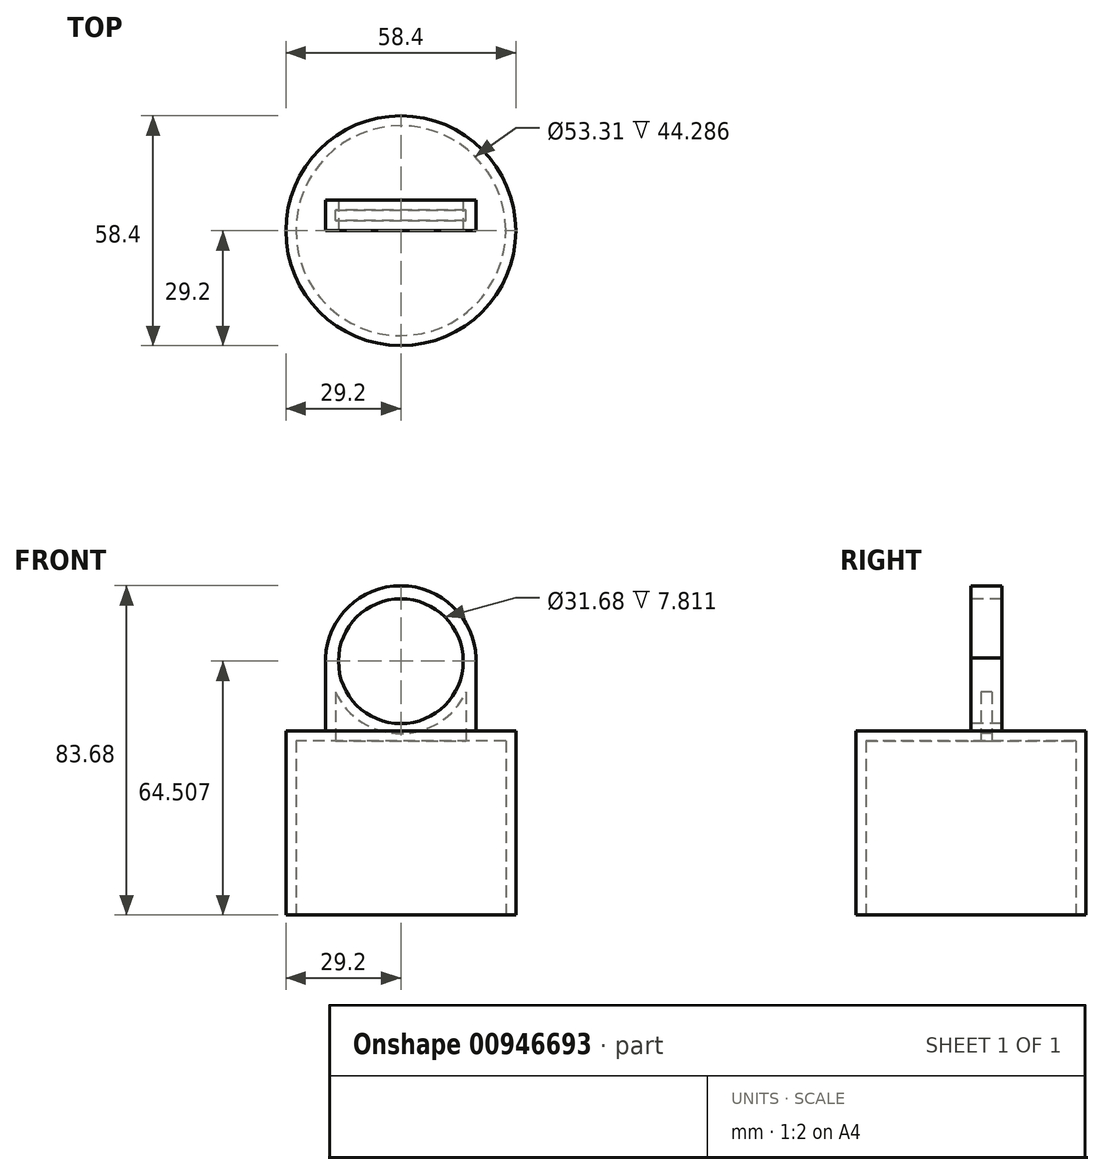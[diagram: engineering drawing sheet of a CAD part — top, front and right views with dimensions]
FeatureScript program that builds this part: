
annotation { "Feature Type Name" : "Feature", "Feature Type Description" : "" }
export const myFeature = defineFeature(function(context is Context, id is Id, definition is map)
    precondition{}
    {
        {
            var Q0;
            Q0=qCreatedBy(makeId("Top.planeOp"),FACE);
            var sketch = newSketch(context, id + "F0", { "sketchPlane" : qUnion([Q0])});
            skCircle(sketch, "E0", {"center": v(0, 0) * mm, "radius": 29.2 * mm});
            skSolve(sketch);
        }
        {
            var Q0;
            Q0=makeQuery(id+"F0.imprint","IMPRINT",FACE,{"disambiguationData":[TD([[makeQuery(id+"F0.imprint","IMPRINT",EDGE,{"derivedFrom":sQuery(id+"F0.wireOp",EDGE,"E0")}),1.0]])]});
            extrude(context, id + "F1", {"entities" : qUnion([Q0]), "depth" : 46.83 * mm, "offsetDistance" : 25.4 * mm});
        }
        {
            var Q0;
            Q0=makeQuery(id+"F1.opExtrude","CAP_FACE",FACE,{"disambiguationData":[OSD([sQuery(id+"F0.wireOp",EDGE,"E0")])],"isStart":false});
            var sketch = newSketch(context, id + "F2", { "sketchPlane" : qUnion([Q0])});
            skLineSegment(sketch, "E1.bottom", {"start": v(-19.15, 0) * mm, "end": v(19.15, 0) * mm});
            skLineSegment(sketch, "E1.top", {"start": v(-19.15, 7.81) * mm, "end": v(19.15, 7.81) * mm});
            skLineSegment(sketch, "E1.left", {"start": v(-19.15, 0) * mm, "end": v(-19.15, 7.81) * mm});
            skLineSegment(sketch, "E1.right", {"start": v(19.15, 0) * mm, "end": v(19.15, 7.81) * mm});
            skSolve(sketch);
        }
        {
            var Q0;
            Q0=makeQuery(id+"F2.imprint","IMPRINT",FACE,{"disambiguationData":[TD([[makeQuery(id+"F2.imprint","IMPRINT",EDGE,{"derivedFrom":sQuery(id+"F2.wireOp",EDGE,"E1.bottom")}),1.0]])]});
            extrude(context, id + "F3", {"entities" : qUnion([Q0]), "operationType" : NewBodyOperationType.ADD, "depth" : 36.92 * mm, "offsetDistance" : 25.4 * mm});
        }
        {
            var Q0;
            Q0=makeQuery(id+"F3.opExtrude","SWEPT_FACE",FACE,{"disambiguationData":[OSD([sQuery(id+"F2.wireOp",EDGE,"E1.bottom")])]});
            var sketch = newSketch(context, id + "F4", { "sketchPlane" : qUnion([Q0])});
            skArc(sketch, "E2", {"start": v(19.15, 65.28) * mm, "mid": v(0, 83.68) * mm, "end": v(-19.15, 65.28) * mm});
            skLineSegment(sketch, "E3", {"start": v(19.15, 65.28) * mm, "end": v(25.18, 65.28) * mm});
            skLineSegment(sketch, "E4", {"start": v(25.18, 65.28) * mm, "end": v(25.18, 92.3) * mm});
            skLineSegment(sketch, "E5", {"start": v(25.18, 92.3) * mm, "end": v(-25.18, 92.3) * mm});
            skLineSegment(sketch, "E6", {"start": v(-25.18, 92.3) * mm, "end": v(-25.18, 65.28) * mm});
            skLineSegment(sketch, "E7", {"start": v(-25.18, 65.28) * mm, "end": v(-19.15, 65.28) * mm});
            skCircle(sketch, "E8", {"center": v(0, 64.5) * mm, "radius": 15.84 * mm});
            skSolve(sketch);
        }
        {
            var Q0;
            Q0=makeQuery(id+"F4.imprint","IMPRINT",FACE,{"disambiguationData":[TD([[makeQuery(id+"F4.imprint","IMPRINT",EDGE,{"derivedFrom":sQuery(id+"F4.wireOp",EDGE,"E8")}),1.0]])]});
            var Q1;
            {var subQ0=sQuery(id+"F4.wireOp",EDGE,"E2");Q1=makeQuery(id+"F4.imprint","IMPRINT",FACE,{"disambiguationData":[TD([[makeQuery(id+"F4.imprint","IMPRINT",EDGE,{"derivedFrom":subQ0}),-1.0]])]});}
            extrude(context, id + "F5", {"entities" : qUnion([Q0, Q1]), "operationType" : NewBodyOperationType.REMOVE, "endBound" : BoundingType.THROUGH_ALL, "oppositeDirection" : true, "depth" : 25.4 * mm, "offsetDistance" : 25.4 * mm});
        }
        {
            var Q0;
            Q0=makeQuery(id+"F1.opExtrude","CAP_FACE",FACE,{"disambiguationData":[OSD([sQuery(id+"F0.wireOp",EDGE,"E0")])],"isStart":true});
            shell(context, id + "F6", {"entities" : qUnion([Q0]), "thickness" : 2.54 * mm});
        }
    });
